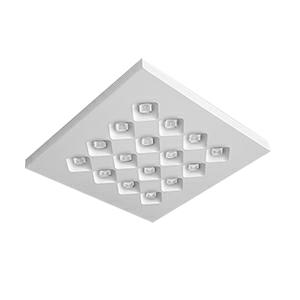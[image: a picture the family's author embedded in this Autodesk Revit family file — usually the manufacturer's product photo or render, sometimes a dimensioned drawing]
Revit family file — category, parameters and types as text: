
# Revit family: 3f_filippi_-_3f_diagon_soft_ugr_3f_filippi_-_23813_a0686_-_3f_diagon_25w-840_ep_soft_ugr_596x596___corn_plaf__ce6d
name_source: partatom
category: Lighting Fixtures
units: mm (PartAtom-declared; Revit-internal decimal feet)

## family parameters
Cut with Voids When Loaded = No
Host = Face
Light Source = No
Part Type = Normal
Room Calculation Point = No
Round Connector Dimension = Use Diameter
Shared = No

## types (1)
- 3F Filippi - 3F Dìagon Soft UGR (1 x LED, 3679 lm, 29 W, 4000 K)
    Apparent Load = 29 VA
    Approval mark = ENEC
    CIE Flux Codes = 59 92 100 100 100
    Color Rendering = 80
    Color Temperature = 4000 K
    Control Gear = Electronic ballast
    Default Elevation = 1800 mm
    Description = ILLUMINOTECHNICAL
Luminous efficiency 100% (DLOR 100%, ULOR 0%).
Initial luminous flux of the luminaire 3679 lm.
Emergency luminaire luminous flux BLF 19.8%.
Direct symmetric distribution.
Installation Interdistance Transv.D = 1.23 x hu - Long.D = 1.23 x hu.
Average luminance <3000 cd/m² for radial angles >65°.
Tabular UGR (CIE 117 - 4H-8H; S=0.25H; 70/50/20): RUG 18.7 - 18.7.
Beam angle: 102° - 101°.
Luminous efficacy 127 lm/W.
Lifetime (L95/B10): 30000 h. (tq+25°C)
Lifetime (L90/B10): 50000 h. (tq+25°C)
Lifetime (L80/B10): 80000 h. (tq+25°C)
Lifetime (L75/B10): 100000 h. (tq+25°C)
Sudden decreased luminous flux after 50000 hours: 0% (C0).
Photobiological safety in compliance with IEC/TR 62778: RG0 risk exempt, (IEC 62471).
In compliance with IEC/EN 62722-2-1 - IEC/EN 62717 standards.

SOURCE
Squared LED module 25W/840.
Energy efficiency class (UE 2019/2020 - UE 2019/2015): C.
CIE 13.3 Colour rendering index: CRI >80 (R9 <50%).
IES TM-30 Fidelity Index: Rf = 84 Rg = 95.
CCT nominal colour temperature 4000 K.
Colour initial tolerance (MacAdam): SDCM 3.

MECHANICAL
Housing in hot-galvanised steel, painted in white polyester.
Honeycombed diagonal screen in white anti-glare polycarbonate.
Opal methacrylate (PMMA) rhomboid lenses with differentiated, engraved and prismatic surfaces for diffused, soft lighting and excellent visual comfort.
Luminaire with limited surface temperature. - D - (EN 60598-2-24)
Dimensions: 600x600 mm, height 40 mm. Weight 7.02 kg.
IP43 protection degree for exposed part, IP20 for recessed part.
Mechanical strength to impacts IK06 (1 joule).
Glow-wire test resistance 650°C.

ELECTRICAL
Halogen Free electronic wiring 230V-50/60Hz, power factor 0.90, THD <25%, constant output current, class I, 1 driver.
Power of the luminaire 29 W.
CE - IEC 60598-1 - EN 60598-1.
EP maintained emergency wiring on board, 1h duration, 24h recharge; compliant with EN 60598-2-22, excluding high risk areas.
SAFE FLICKER: PstLM=<1 and SVM=<0.4 (IEC TR 61547-1 and IEC TR 63158), to ensure a more comfortable and safe light.
Ambient temperature from +5°C to +25°C.
Temperature class T6 max 85°C.
Quick connection.
Relative humidity UR: <85%.

INSTALLATION
Ceiling.
Height only 40 mm.
All accessories dedicated to this product are available on the Catalog and on our website www.3F-Filippi.com.

ACCESSORIES
A0686 - 596x596 Diagon frame for Ceiling installation.

APPLICATIONS
Environments: staterooms, with VDTs, offices.
Environments with exacting visual tasks, where diffused soft light for optimum visual comfort is required.

WARNING
Luminaire designed for disposal/recycling at end-of-life.
Replaceable (LED only) light source by a professional. Replaceable control gear by a professional.
    Height = 0 mm  [stored 0 ft]
    Lamp = 1 x LED
    Lamp Light Flux = 3679 lm
    Lamp Power = 29 W
    Lamp count = 1
    Length = 600 mm
    Lifetime = 50000 h
    Luminous efficacy = 127 lm/W
    Manufacturer = 3F Filippi
    ModVariant = No
    Model = 3F Filippi - 23813+A0686 - 3F Diagon 25W-840 EP SOFT UGR 596x596 + Corn.plaf.
    Mounting Place = Ceiling
    Mounting Type = Recessed
    Number of Poles = 1
    OnlyDefault = Yes
    Power Factor = 1
    Product Name = 3F Filippi - 3F Dìagon Soft UGR
    Product group = recessed luminaire
    ProductGroupID = 4
    Protection Class = Protection class I
    Protection Degree = IP 20
    RLX_Detail_Level = 1
    RLX_Emergency_Light_Flux = 0 lm
    RLX_Emergency_Type = 0
    RLX_Emergency_Type_DB = No
    RlxData = <blob elided: 95717 chars, md5=70eece71>
    Socket = socket
    Standby Power = 0 W
    System Light Flux = 3679 lm
    System Power = 29 W
    Type Comments = Product without accessories
    Type Image = 3ffilippi_3f_diagon__a0686.jpg
    URL = http://relux.com
    VarID = ---
    Voltage = 0 V
    Weight = 0.00 kg
    Width = 600 mm

note: [stored X ft] marks values corroborated as IEEE doubles in the binary element streams (Revit-internal decimal feet)

## geometry (parser evidence)
native form markers: Blend x4, Sweep x10
no freeform markers — native parametric forms only
